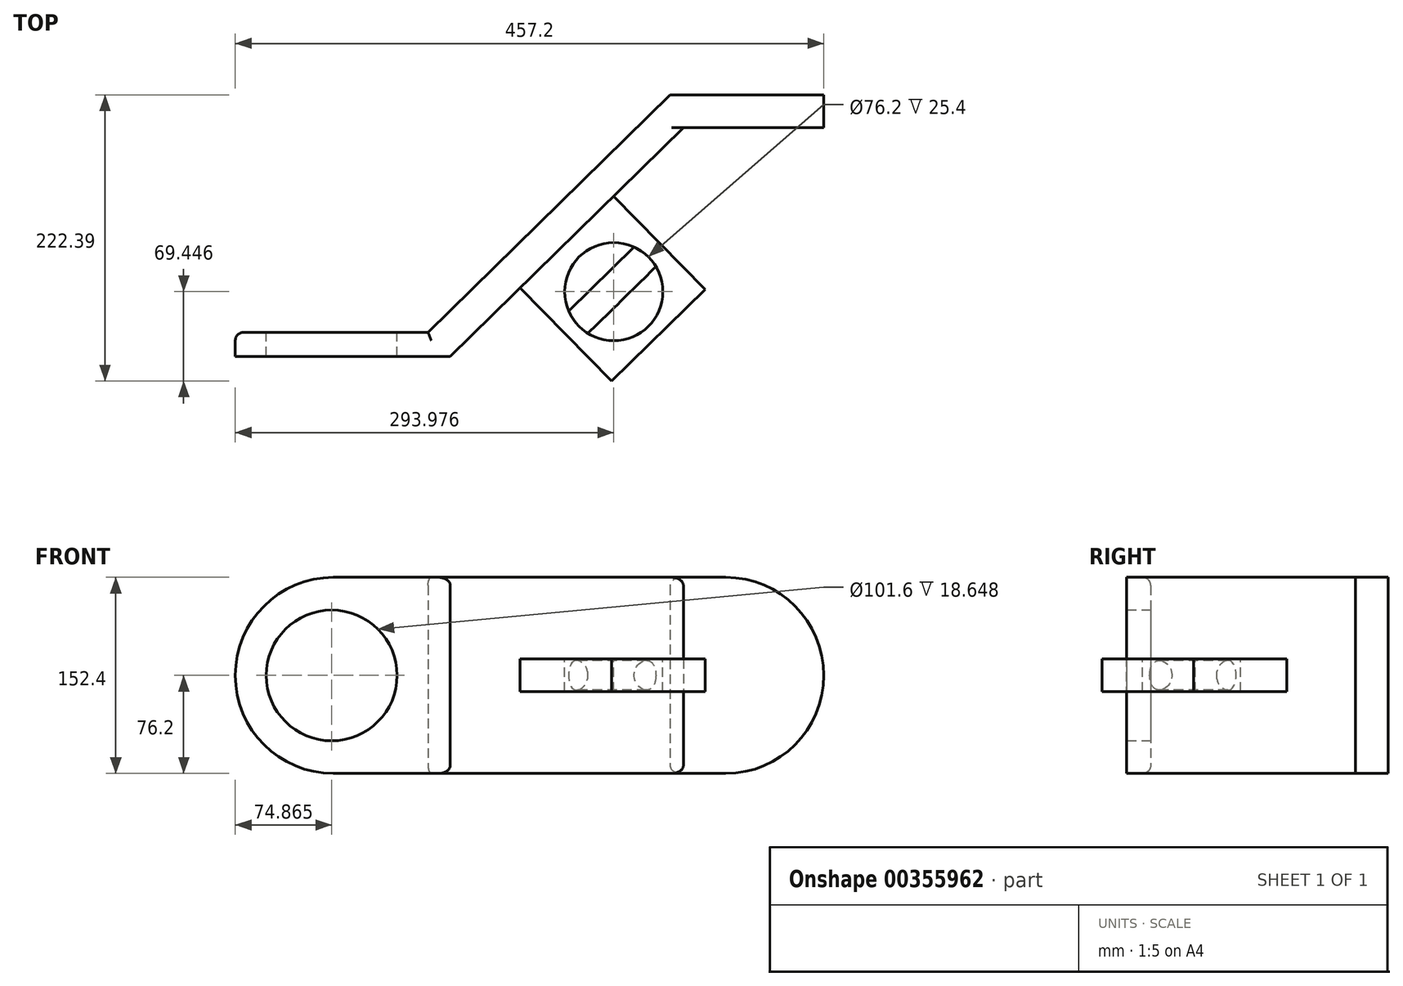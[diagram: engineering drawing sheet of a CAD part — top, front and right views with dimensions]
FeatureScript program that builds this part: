
annotation { "Feature Type Name" : "Feature", "Feature Type Description" : "" }
export const myFeature = defineFeature(function(context is Context, id is Id, definition is map)
    precondition{}
    {
        {
            var Q0;
            Q0=qCreatedBy(makeId("Top.planeOp"),FACE);
            var sketch = newSketch(context, id + "F0", { "sketchPlane" : qUnion([Q0])});
            skLineSegment(sketch, "E0.bottom", {"start": v(228.6, -101.6) * mm, "end": v(-228.6, -101.6) * mm});
            skLineSegment(sketch, "E0.top", {"start": v(228.6, 101.6) * mm, "end": v(-228.6, 101.6) * mm});
            skLineSegment(sketch, "E0.left", {"start": v(228.6, -101.6) * mm, "end": v(228.6, 101.6) * mm});
            skLineSegment(sketch, "E0.right", {"start": v(-228.6, -101.6) * mm, "end": v(-228.6, 101.6) * mm});
            skPoint(sketch, "E0.middle", {"position": v(0, 0) * mm});
            skLineSegment(sketch, "E1", {"start": v(228.6, 101.6) * mm, "end": v(36.67, 101.6) * mm});
            skLineSegment(sketch, "E2", {"start": v(-78.87, -82.95) * mm, "end": v(-228.6, -82.95) * mm});
            skLineSegment(sketch, "E3", {"start": v(-78.87, -82.95) * mm, "end": v(109.12, 101.6) * mm});
            skLineSegment(sketch, "E4.0", {"start": v(228.6, 76.2) * mm, "end": v(119.5, 76.2) * mm});
            skLineSegment(sketch, "E5.0", {"start": v(-61.6, -101.6) * mm, "end": v(121.27, 77.93) * mm});
            skSolve(sketch);
        }
        {
            var Q0;
            {var subQ7=sQuery(id+"F0.wireOp",EDGE,"E2");Q0=makeQuery(id+"F0.imprint","IMPRINT",FACE,{"disambiguationData":[TD([[makeQuery(id+"F0.imprint","IMPRINT",EDGE,{"derivedFrom":subQ7}),1.0]])]});}
            extrude(context, id + "F1", {"entities" : qUnion([Q0]), "depth" : 152.4 * mm});
        }
        {
            var Q0;
            Q0=makeQuery(id+"F1.opExtrude","SWEPT_FACE",FACE,{"disambiguationData":[OSD([sQuery(id+"F0.wireOp",EDGE,"E1")])]});
            var sketch = newSketch(context, id + "F2", { "sketchPlane" : qUnion([Q0])});
            skCircle(sketch, "E6", {"center": v(-168.86, 76.2) * mm, "radius": 38.1 * mm});
            skPoint(sketch, "E6.centerSnap0", {"position": v(-168.86, 0) * mm});
            skPoint(sketch, "E6.centerSnap1", {"position": v(-228.6, 76.2) * mm});
            skSolve(sketch);
        }
        {
            var Q0;
            Q0=makeQuery(id+"F1.opExtrude","SWEPT_FACE",FACE,{"disambiguationData":[OSD([sQuery(id+"F0.wireOp",EDGE,"E2")])]});
            var sketch = newSketch(context, id + "F3", { "sketchPlane" : qUnion([Q0])});
            skCircle(sketch, "E7", {"center": v(153.74, 76.2) * mm, "radius": 50.8 * mm});
            skPoint(sketch, "E7.centerSnap0", {"position": v(228.6, 76.2) * mm});
            skPoint(sketch, "E7.centerSnap1", {"position": v(153.74, 0) * mm});
            skSolve(sketch);
        }
        {
            var Q0;
            Q0=makeQuery(id+"F1.opExtrude","CAP_EDGE",EDGE,{"disambiguationData":[OSD([sQuery(id+"F0.wireOp",EDGE,"E0.left")])],"isStart":true});
            var Q1;
            Q1=makeQuery(id+"F1.opExtrude","CAP_EDGE",EDGE,{"disambiguationData":[OSD([sQuery(id+"F0.wireOp",EDGE,"E0.left")])],"isStart":false});
            fillet(context, id + "F4", {"entities" : qUnion([Q0, Q1]), "radius" : 76.2 * mm, "tangentPropagation" : true, "allowEdgeOverflow" : false});
        }
        {
            var Q0;
            Q0=makeQuery(id+"F1.opExtrude","CAP_EDGE",EDGE,{"disambiguationData":[OSD([sQuery(id+"F0.wireOp",EDGE,"E0.right")])],"isStart":false});
            var Q1;
            Q1=makeQuery(id+"F1.opExtrude","CAP_EDGE",EDGE,{"disambiguationData":[OSD([sQuery(id+"F0.wireOp",EDGE,"E0.right")])],"isStart":true});
            fillet(context, id + "F5", {"entities" : qUnion([Q0, Q1]), "radius" : 76.2 * mm, "tangentPropagation" : true, "allowEdgeOverflow" : false});
        }
        {
            var Q0;
            Q0=makeQuery(id+"F3.imprint","IMPRINT",FACE,{"disambiguationData":[TD([[makeQuery(id+"F3.imprint","IMPRINT",EDGE,{"derivedFrom":sQuery(id+"F3.wireOp",EDGE,"E7")}),1.0]])]});
            var Q1;
            Q1=makeQuery(id+"F2.imprint","IMPRINT",FACE,{"disambiguationData":[TD([[makeQuery(id+"F2.imprint","IMPRINT",EDGE,{"derivedFrom":sQuery(id+"F2.wireOp",EDGE,"E6")}),1.0]])]});
            extrude(context, id + "F6", {"entities" : qUnion([Q0, Q1]), "operationType" : NewBodyOperationType.REMOVE, "endBound" : BoundingType.THROUGH_ALL, "oppositeDirection" : true, "depth" : 25.4 * mm});
        }
        {
            var Q0;
            Q0=makeQuery(id+"F1.opExtrude","CAP_EDGE",EDGE,{"disambiguationData":[OSD([sQuery(id+"F0.wireOp",EDGE,"E3")])],"isStart":true});
            var Q1;
            Q1=makeQuery(id+"F1.opExtrude","CAP_EDGE",EDGE,{"disambiguationData":[OSD([sQuery(id+"F0.wireOp",EDGE,"E1")])],"isStart":true});
            var Q2;
            Q2=makeQuery(id+"F4.opFillet","BLEND_EDGE",EDGE,{"blendedFrom":[makeQuery(id+"F1.opExtrude","CAP_EDGE",EDGE,{"disambiguationData":[OSD([sQuery(id+"F0.wireOp",EDGE,"E0.left")])],"isStart":false}),makeQuery(id+"F1.opExtrude","SWEPT_FACE",FACE,{"disambiguationData":[OSD([sQuery(id+"F0.wireOp",EDGE,"E1")])]})],"blendedInto":[makeQuery(id+"F1.opExtrude","SWEPT_FACE",FACE,{"disambiguationData":[OSD([sQuery(id+"F0.wireOp",EDGE,"E1")])]})]});
            var Q3;
            Q3=makeQuery(id+"F1.opExtrude","CAP_EDGE",EDGE,{"disambiguationData":[OSD([sQuery(id+"F0.wireOp",EDGE,"E1")])],"isStart":false});
            var Q4;
            Q4=makeQuery(id+"F1.opExtrude","CAP_EDGE",EDGE,{"disambiguationData":[OSD([sQuery(id+"F0.wireOp",EDGE,"E3")])],"isStart":false});
            var Q5;
            Q5=makeQuery(id+"F1.opExtrude","CAP_EDGE",EDGE,{"disambiguationData":[OSD([sQuery(id+"F0.wireOp",EDGE,"E2")])],"isStart":false});
            var Q6;
            Q6=makeQuery(id+"F5.opFillet","BLEND_EDGE",EDGE,{"blendedFrom":[makeQuery(id+"F1.opExtrude","CAP_EDGE",EDGE,{"disambiguationData":[OSD([sQuery(id+"F0.wireOp",EDGE,"E0.right")])],"isStart":false}),makeQuery(id+"F1.opExtrude","SWEPT_FACE",FACE,{"disambiguationData":[OSD([sQuery(id+"F0.wireOp",EDGE,"E2")])]})],"blendedInto":[makeQuery(id+"F1.opExtrude","SWEPT_FACE",FACE,{"disambiguationData":[OSD([sQuery(id+"F0.wireOp",EDGE,"E2")])]})]});
            var Q7;
            Q7=makeQuery(id+"F5.opFillet","BLEND_EDGE",EDGE,{"blendedFrom":[makeQuery(id+"F1.opExtrude","CAP_EDGE",EDGE,{"disambiguationData":[OSD([sQuery(id+"F0.wireOp",EDGE,"E0.right")])],"isStart":false}),makeQuery(id+"F1.opExtrude","SWEPT_FACE",FACE,{"disambiguationData":[OSD([sQuery(id+"F0.wireOp",EDGE,"E0.bottom")])]})],"blendedInto":[makeQuery(id+"F1.opExtrude","SWEPT_FACE",FACE,{"disambiguationData":[OSD([sQuery(id+"F0.wireOp",EDGE,"E0.bottom")])]})]});
            var Q8;
            Q8=makeQuery(id+"F1.opExtrude","CAP_EDGE",EDGE,{"disambiguationData":[OSD([sQuery(id+"F0.wireOp",EDGE,"E5.0")])],"isStart":true});
            var Q9;
            Q9=makeQuery(id+"F4.opFillet","BLEND_EDGE",EDGE,{"blendedFrom":[makeQuery(id+"F1.opExtrude","CAP_EDGE",EDGE,{"disambiguationData":[OSD([sQuery(id+"F0.wireOp",EDGE,"E0.left")])],"isStart":false}),makeQuery(id+"F1.opExtrude","SWEPT_FACE",FACE,{"disambiguationData":[OSD([sQuery(id+"F0.wireOp",EDGE,"E4.0")])]})],"blendedInto":[makeQuery(id+"F1.opExtrude","SWEPT_FACE",FACE,{"disambiguationData":[OSD([sQuery(id+"F0.wireOp",EDGE,"E4.0")])]})]});
            var Q10;
            Q10=makeQuery(id+"F1.opExtrude","CAP_EDGE",EDGE,{"disambiguationData":[OSD([sQuery(id+"F0.wireOp",EDGE,"E5.0")])],"isStart":false});
            fillet(context, id + "F7", {"entities" : qUnion([Q0, Q1, Q2, Q3, Q4, Q5, Q6, Q7, Q8, Q9, Q10]), "radius" : 6.35 * mm, "tangentPropagation" : true, "allowEdgeOverflow" : false});
        }
        {
            var Q0;
            Q0=makeQuery(id+"F1.opExtrude","SWEPT_FACE",FACE,{"disambiguationData":[OSD([sQuery(id+"F0.wireOp",EDGE,"E5.0")])]});
            var sketch = newSketch(context, id + "F8", { "sketchPlane" : qUnion([Q0])});
            skLineSegment(sketch, "E8.bottom", {"start": v(62.56, 63.5) * mm, "end": v(-39.04, 63.5) * mm});
            skLineSegment(sketch, "E8.top", {"start": v(62.56, 88.9) * mm, "end": v(-39.04, 88.9) * mm});
            skLineSegment(sketch, "E8.left", {"start": v(62.56, 63.5) * mm, "end": v(62.56, 88.9) * mm});
            skLineSegment(sketch, "E8.right", {"start": v(-39.04, 63.5) * mm, "end": v(-39.04, 88.9) * mm});
            skPoint(sketch, "E8.middle", {"position": v(11.76, 76.2) * mm});
            skPoint(sketch, "E8.middle.positionSnap0", {"position": v(-115.14, 76.2) * mm});
            skPoint(sketch, "E8.middle.positionSnap1", {"position": v(11.76, 6.35) * mm});
            skPoint(sketch, "E8.centerSnap0", {"position": v(-115.14, 76.2) * mm});
            skPoint(sketch, "E8.centerSnap1", {"position": v(11.76, 6.35) * mm});
            skSolve(sketch);
        }
        {
            var Q0;
            Q0=makeQuery(id+"F8.imprint","IMPRINT",FACE,{"disambiguationData":[TD([[makeQuery(id+"F8.imprint","IMPRINT",EDGE,{"derivedFrom":sQuery(id+"F8.wireOp",EDGE,"E8.bottom")}),-1.0]])]});
            extrude(context, id + "F9", {"entities" : qUnion([Q0]), "operationType" : NewBodyOperationType.ADD, "depth" : 101.6 * mm});
        }
        {
            var Q0;
            Q0=makeQuery(id+"F9.opExtrude","SWEPT_FACE",FACE,{"disambiguationData":[OSD([sQuery(id+"F8.wireOp",EDGE,"E8.top")])]});
            var sketch = newSketch(context, id + "F10", { "sketchPlane" : qUnion([Q0])});
            skCircle(sketch, "E9", {"center": v(65.38, -51.34) * mm, "radius": 38.1 * mm});
            skSolve(sketch);
        }
        {
            var Q0;
            Q0=makeQuery(id+"F9.opExtrude","SWEPT_FACE",FACE,{"disambiguationData":[OSD([sQuery(id+"F8.wireOp",EDGE,"E8.right")])]});
            var sketch = newSketch(context, id + "F11", { "sketchPlane" : qUnion([Q0])});
            skCircle(sketch, "E10", {"center": v(80.14, 76.31) * mm, "radius": 11.43 * mm});
            skPoint(sketch, "E10.centerSnap0", {"position": v(80.14, 63.5) * mm});
            skSolve(sketch);
        }
        {
            var Q0;
            Q0=makeQuery(id+"F10.imprint","IMPRINT",FACE,{"disambiguationData":[TD([[makeQuery(id+"F10.imprint","IMPRINT",EDGE,{"derivedFrom":sQuery(id+"F10.wireOp",EDGE,"E9")}),1.0]])]});
            extrude(context, id + "F12", {"entities" : qUnion([Q0]), "operationType" : NewBodyOperationType.REMOVE, "oppositeDirection" : true, "depth" : 25.4 * mm});
        }
        {
            var Q0;
            Q0=makeQuery(id+"F11.imprint","IMPRINT",FACE,{"disambiguationData":[TD([[makeQuery(id+"F11.imprint","IMPRINT",EDGE,{"derivedFrom":sQuery(id+"F11.wireOp",EDGE,"E10")}),1.0]])]});
            extrude(context, id + "F13", {"entities" : qUnion([Q0]), "operationType" : NewBodyOperationType.ADD, "oppositeDirection" : true, "depth" : 95.25 * mm});
        }
    });
